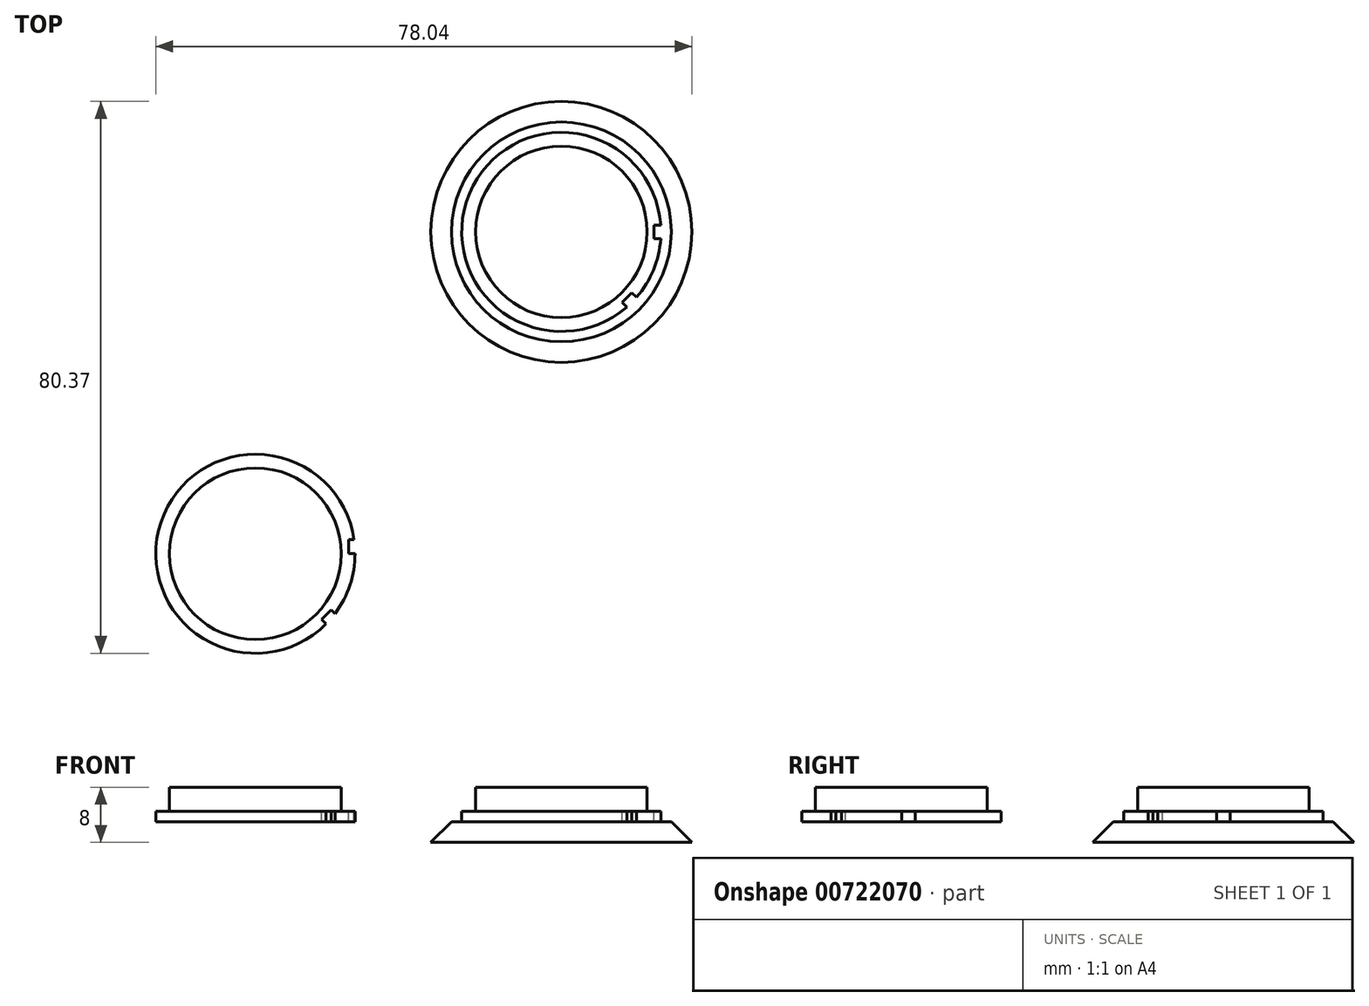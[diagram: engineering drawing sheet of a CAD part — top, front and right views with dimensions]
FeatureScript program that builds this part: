
annotation { "Feature Type Name" : "Feature", "Feature Type Description" : "" }
export const myFeature = defineFeature(function(context is Context, id is Id, definition is map)
    precondition{}
    {
        {
            var Q0;
            Q0=qCreatedBy(makeId("Top.planeOp"),FACE);
            var sketch = newSketch(context, id + "F0", { "sketchPlane" : qUnion([Q0])});
            skCircle(sketch, "E0", {"center": v(0, 0) * mm, "radius": 19 * mm});
            skSolve(sketch);
        }
        {
            var Q0;
            Q0=qCreatedBy(makeId("Top.planeOp"),FACE);
            cPlane(context, id + "F1", {"entities" : qUnion([Q0]), "cplaneType" : CPlaneType.OFFSET, "offset" : 3 * mm, "width" : 152.4 * mm, "height" : 152.4 * mm});
        }
        {
            var Q0;
            Q0=qCreatedBy(id+"F1.planeOp",FACE);
            var sketch = newSketch(context, id + "F2", { "sketchPlane" : qUnion([Q0])});
            skCircle(sketch, "E1", {"center": v(0, 0) * mm, "radius": 16 * mm});
            skSolve(sketch);
        }
        {
            var Q0;
            Q0=makeQuery(id+"F0.imprint","IMPRINT",FACE,{"disambiguationData":[TD([[makeQuery(id+"F0.imprint","IMPRINT",EDGE,{"derivedFrom":sQuery(id+"F0.wireOp",EDGE,"E0")}),1.0]])]});
            var Q1;
            Q1=makeQuery(id+"F2.imprint","IMPRINT",FACE,{"disambiguationData":[TD([[makeQuery(id+"F2.imprint","IMPRINT",EDGE,{"derivedFrom":sQuery(id+"F2.wireOp",EDGE,"E1")}),1.0]])]});
            loft(context, id + "F3", {"sheetProfilesArray" : [{ "sheetProfileEntities" : qUnion([Q0]) }, { "sheetProfileEntities" : qUnion([Q1]) }]});
        }
        {
            var Q0;
            Q0=makeQuery(id+"F3.opLoft","CAP_FACE",FACE,{"disambiguationData":[OSD([makeQuery(id+"F2.imprint","IMPRINT",FACE,{"disambiguationData":[TD([[makeQuery(id+"F2.imprint","IMPRINT",EDGE,{"derivedFrom":sQuery(id+"F2.wireOp",EDGE,"E1")}),1.0]])]})])],"isStart":true});
            var sketch = newSketch(context, id + "F4", { "sketchPlane" : qUnion([Q0])});
            skCircle(sketch, "E2", {"center": v(0, 0) * mm, "radius": 14.5 * mm});
            skSolve(sketch);
        }
        {
            var Q0;
            Q0=makeQuery(id+"F4.imprint","IMPRINT",FACE,{"disambiguationData":[TD([[makeQuery(id+"F4.imprint","IMPRINT",EDGE,{"derivedFrom":sQuery(id+"F4.wireOp",EDGE,"E2")}),1.0]])]});
            extrude(context, id + "F5", {"entities" : qUnion([Q0]), "operationType" : NewBodyOperationType.ADD, "depth" : 1.5 * mm, "offsetDistance" : 25.4 * mm});
        }
        {
            var Q0;
            Q0=makeQuery(id+"F5.opExtrude","CAP_FACE",FACE,{"disambiguationData":[OSD([sQuery(id+"F4.wireOp",EDGE,"E2")])],"isStart":false});
            var sketch = newSketch(context, id + "F6", { "sketchPlane" : qUnion([Q0])});
            skCircle(sketch, "E3", {"center": v(0, 0) * mm, "radius": 12.49 * mm});
            skSolve(sketch);
        }
        {
            var Q0;
            Q0=makeQuery(id+"F6.imprint","IMPRINT",FACE,{"disambiguationData":[TD([[makeQuery(id+"F6.imprint","IMPRINT",EDGE,{"derivedFrom":sQuery(id+"F6.wireOp",EDGE,"E3")}),1.0]])]});
            extrude(context, id + "F7", {"entities" : qUnion([Q0]), "operationType" : NewBodyOperationType.ADD, "depth" : 3.5 * mm, "offsetDistance" : 25.4 * mm});
        }
        {
            var Q0;
            Q0=makeQuery(id+"F5.opExtrude","CAP_FACE",FACE,{"disambiguationData":[OSD([sQuery(id+"F4.wireOp",EDGE,"E2")])],"isStart":false});
            var sketch = newSketch(context, id + "F8", { "sketchPlane" : qUnion([Q0])});
            skLineSegment(sketch, "E4.bottom", {"start": v(13.5, 1) * mm, "end": v(14.56, 1) * mm});
            skLineSegment(sketch, "E4.top", {"start": v(13.5, -1) * mm, "end": v(14.56, -1) * mm});
            skLineSegment(sketch, "E4.left", {"start": v(13.5, 1) * mm, "end": v(13.5, -1) * mm});
            skLineSegment(sketch, "E4.right", {"start": v(14.56, 1) * mm, "end": v(14.56, -1) * mm});
            skPoint(sketch, "E5.center", {"position": v(0, 0) * mm});
            skLineSegment(sketch, "E6.1.0", {"start": v(10.26, -8.84) * mm, "end": v(11, -9.6) * mm});
            skLineSegment(sketch, "E6.1.1", {"start": v(10.26, -8.84) * mm, "end": v(8.84, -10.26) * mm});
            skLineSegment(sketch, "E6.1.2", {"start": v(8.84, -10.26) * mm, "end": v(9.6, -11) * mm});
            skLineSegment(sketch, "E6.1.3", {"start": v(11, -9.6) * mm, "end": v(9.6, -11) * mm});
            skLineSegment(sketch, "E6.anchor1", {"start": v(0, 0) * mm, "end": v(13.5, -1) * mm, "construction": true});
            skLineSegment(sketch, "E6.anchor2", {"start": v(0, 0) * mm, "end": v(8.84, -10.26) * mm, "construction": true});
            skSolve(sketch);
        }
        {
            var Q0;
            {var subQ0=sQuery(id+"F8.wireOp",EDGE,"E6.1.1");Q0=makeQuery(id+"F8.imprint","IMPRINT",FACE,{"disambiguationData":[TD([[makeQuery(id+"F8.imprint","IMPRINT",EDGE,{"derivedFrom":subQ0}),1.0]])]});}
            var Q1;
            {var subQ0=sQuery(id+"F8.wireOp",EDGE,"E4.left");Q1=makeQuery(id+"F8.imprint","IMPRINT",FACE,{"disambiguationData":[TD([[makeQuery(id+"F8.imprint","IMPRINT",EDGE,{"derivedFrom":subQ0}),1.0]])]});}
            extrude(context, id + "F9", {"entities" : qUnion([Q0, Q1]), "operationType" : NewBodyOperationType.REMOVE, "depth" : -1.5 * mm, "offsetDistance" : 25.4 * mm});
        }
        {
            var Q0;
            Q0=qCreatedBy(id+"F1.planeOp",FACE);
            var sketch = newSketch(context, id + "F10", { "sketchPlane" : qUnion([Q0])});
            skCircle(sketch, "E7", {"center": v(-44.54, -46.87) * mm, "radius": 14.5 * mm});
            skSolve(sketch);
        }
        {
            var Q0;
            Q0=makeQuery(id+"F10.imprint","IMPRINT",FACE,{"disambiguationData":[TD([[makeQuery(id+"F10.imprint","IMPRINT",EDGE,{"derivedFrom":sQuery(id+"F10.wireOp",EDGE,"E7")}),1.0]])]});
            extrude(context, id + "F11", {"entities" : qUnion([Q0]), "depth" : 1.5 * mm, "offsetDistance" : 25.4 * mm});
        }
        {
            var Q0;
            Q0=makeQuery(id+"F11.opExtrude","CAP_FACE",FACE,{"disambiguationData":[OSD([sQuery(id+"F10.wireOp",EDGE,"E7")])],"isStart":false});
            var sketch = newSketch(context, id + "F12", { "sketchPlane" : qUnion([Q0])});
            skCircle(sketch, "E8", {"center": v(-44.54, -46.87) * mm, "radius": 12.5 * mm});
            skSolve(sketch);
        }
        {
            var Q0;
            Q0=makeQuery(id+"F12.imprint","IMPRINT",FACE,{"disambiguationData":[TD([[makeQuery(id+"F12.imprint","IMPRINT",EDGE,{"derivedFrom":sQuery(id+"F12.wireOp",EDGE,"E8")}),1.0]])]});
            extrude(context, id + "F13", {"entities" : qUnion([Q0]), "operationType" : NewBodyOperationType.ADD, "depth" : 3.5 * mm, "offsetDistance" : 25.4 * mm});
        }
        {
            var Q0;
            Q0=makeQuery(id+"F11.opExtrude","CAP_FACE",FACE,{"disambiguationData":[OSD([sQuery(id+"F10.wireOp",EDGE,"E7")])],"isStart":false});
            var sketch = newSketch(context, id + "F14", { "sketchPlane" : qUnion([Q0])});
            skLineSegment(sketch, "E9.bottom", {"start": v(-30.98, -44.83) * mm, "end": v(-29.62, -44.83) * mm});
            skLineSegment(sketch, "E9.top", {"start": v(-30.98, -46.83) * mm, "end": v(-29.62, -46.83) * mm});
            skLineSegment(sketch, "E9.left", {"start": v(-30.98, -44.83) * mm, "end": v(-30.98, -46.83) * mm});
            skLineSegment(sketch, "E9.right", {"start": v(-29.62, -44.83) * mm, "end": v(-29.62, -46.83) * mm});
            skLineSegment(sketch, "E10.1.0", {"start": v(-33.5, -55.02) * mm, "end": v(-32.55, -55.97) * mm});
            skLineSegment(sketch, "E10.1.1", {"start": v(-32.55, -55.97) * mm, "end": v(-33.97, -57.39) * mm});
            skLineSegment(sketch, "E10.1.2", {"start": v(-33.5, -55.02) * mm, "end": v(-34.92, -56.43) * mm});
            skLineSegment(sketch, "E10.1.3", {"start": v(-34.92, -56.43) * mm, "end": v(-33.97, -57.39) * mm});
            skPoint(sketch, "E10.center", {"position": v(-44.54, -46.87) * mm});
            skLineSegment(sketch, "E10.anchor1", {"start": v(-44.54, -46.87) * mm, "end": v(-30.98, -46.83) * mm, "construction": true});
            skLineSegment(sketch, "E10.anchor2", {"start": v(-44.54, -46.87) * mm, "end": v(-34.92, -56.43) * mm, "construction": true});
            skSolve(sketch);
        }
        {
            var Q0;
            {var subQ0=sQuery(id+"F14.wireOp",EDGE,"E10.1.2");Q0=makeQuery(id+"F14.imprint","IMPRINT",FACE,{"disambiguationData":[TD([[makeQuery(id+"F14.imprint","IMPRINT",EDGE,{"derivedFrom":subQ0}),1.0]])]});}
            var Q1;
            {var subQ0=sQuery(id+"F14.wireOp",EDGE,"E9.left");Q1=makeQuery(id+"F14.imprint","IMPRINT",FACE,{"disambiguationData":[TD([[makeQuery(id+"F14.imprint","IMPRINT",EDGE,{"derivedFrom":subQ0}),1.0]])]});}
            extrude(context, id + "F15", {"entities" : qUnion([Q0, Q1]), "operationType" : NewBodyOperationType.REMOVE, "oppositeDirection" : true, "depth" : 1.5 * mm, "offsetDistance" : 25.4 * mm});
        }
    });
